# Revit family: Deca_Misturador Lavatório Dot_1874.C.DOT_Parede Horizontal
name_source: partatom
category: Plumbing Fixtures
revit_build: Autodesk Revit Architecture 2012 (Build: 20120126_0600(x64)
units: mm (PartAtom-declared; Revit-internal decimal feet)

## types (2) — shared parameters
Acompanha o Produto = Válvula de escoamento 1601.C
Aprovado por = Contino/quattroD
Assembly Code = D2020
Atendimento ao Cliente = 0800-0117073
Consumo = Varia com a pressão
Criado por = Contino/quattroD
Código = 1874.C.DOT
Default Elevation = 800 mm  [stored 2.62467 ft]
Description = Misturador Lavatório Parede
Diâmetro Água Fria = 15 mm  [stored 0.0492126 ft]
Diâmetro Água Quente = 15 mm  [stored 0.0492126 ft]
Flow Pressure = 0.00 psi
Informações Complementares = Mecanismo: 1/4 de volta
Linha = Dot
Louça/Metais = Metal
Manufacturer = Deca
Material = Deca_Latão Cromado e Plástico de Engenharia
Misturador = Deca CR10 Cromado Metal
Model = 1874.C.DOT
Norma = ABNT NBR 14390: 2001
Peso Liquido (Kg) = 5.78
Pressão = 2 A 40 mca
Produto = Misturador Lavatório Parede Horizontal Dot
Raio Água Fria = 8 mm  [stored 0.0262467 ft]
Raio Água Quente = 8 mm  [stored 0.0262467 ft]
Segmento = Luxo
URL = www.deca.com.br/produtos
Variações de COR = Cromado (1874.C.DOT); Cromado/Branco (1874.C.DOT.BR)
zero-valued in all types: CWFU, HWFU, WFU

## per-type parameters (varying)
| type | Acessório |
| 1874.C.DOT_Cromado CR10 | Deca CR10 Cromado Metal |
| 1874.C.DOT.BR_Cromado CR10/Branco BR16 | Deca BR 16 Branco Metal |

note: [stored X ft] marks values corroborated as IEEE doubles in the binary element streams (Revit-internal decimal feet)

## geometry (parser evidence)
native form markers: Blend x2, Sweep x2
no freeform markers — native parametric forms only
